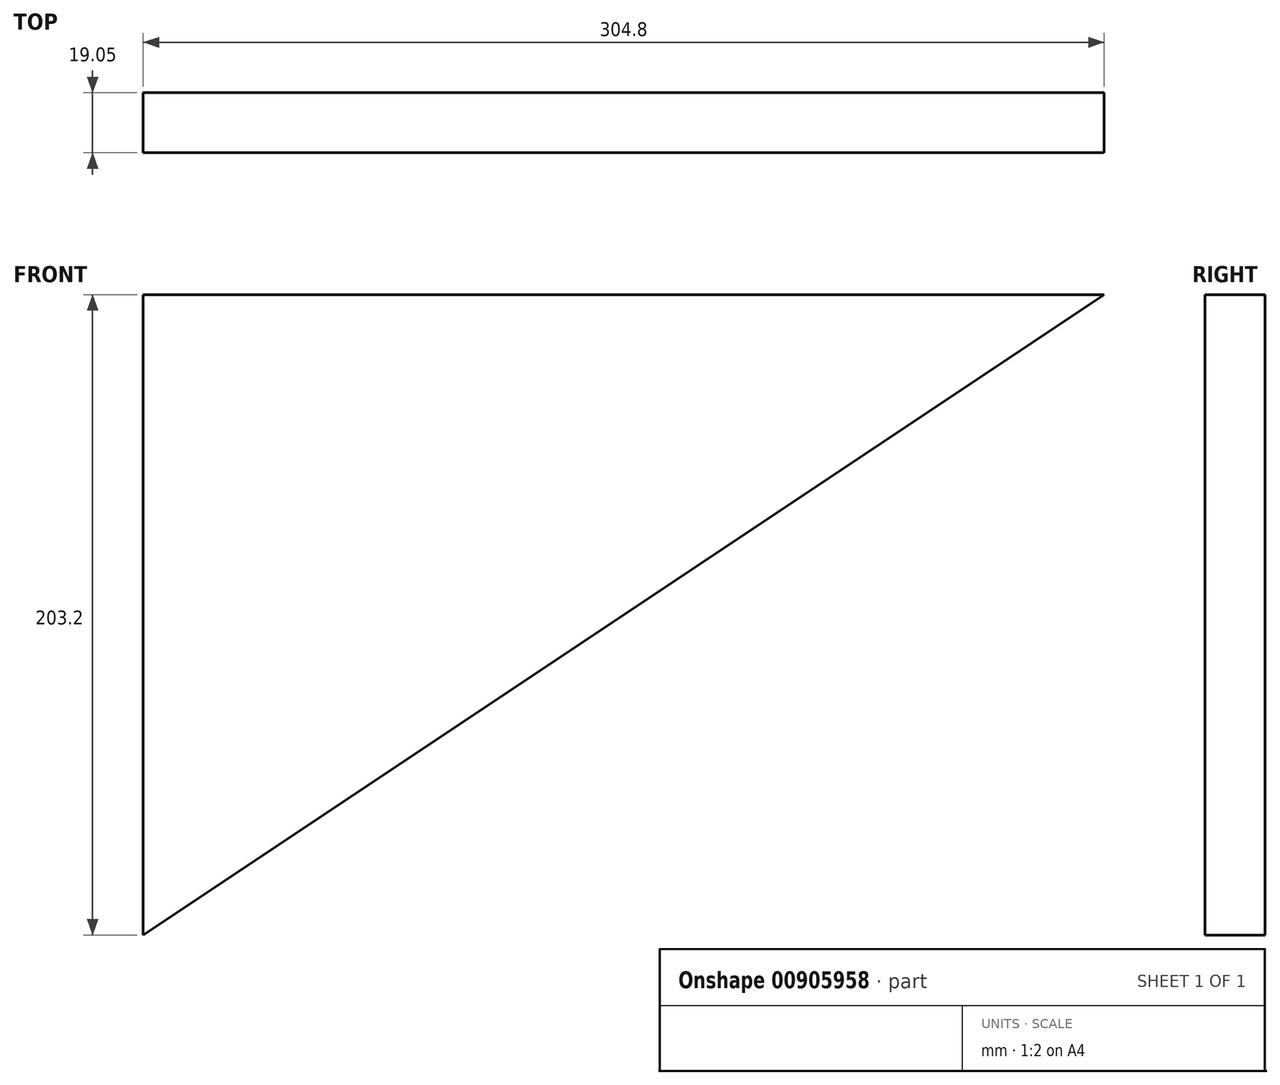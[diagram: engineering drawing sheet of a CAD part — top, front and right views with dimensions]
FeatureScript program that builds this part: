
annotation { "Feature Type Name" : "Feature", "Feature Type Description" : "" }
export const myFeature = defineFeature(function(context is Context, id is Id, definition is map)
    precondition{}
    {
        {
            var Q0;
            Q0=qCreatedBy(makeId("Front.planeOp"),FACE);
            var sketch = newSketch(context, id + "F0", { "sketchPlane" : qUnion([Q0])});
            skLineSegment(sketch, "E0", {"start": v(0, 0) * mm, "end": v(0, 203.2) * mm});
            skLineSegment(sketch, "E1", {"start": v(0, 203.2) * mm, "end": v(304.8, 203.2) * mm});
            skLineSegment(sketch, "E2", {"start": v(304.8, 203.2) * mm, "end": v(0, 0) * mm});
            skSolve(sketch);
        }
        {
            var Q0;
            Q0 = qSketchRegion(id + "F0", true);
            extrude(context, id + "F1", {"entities" : qUnion([Q0]), "depth" : 19.05 * mm, "offsetDistance" : 25.4 * mm});
        }
    });
